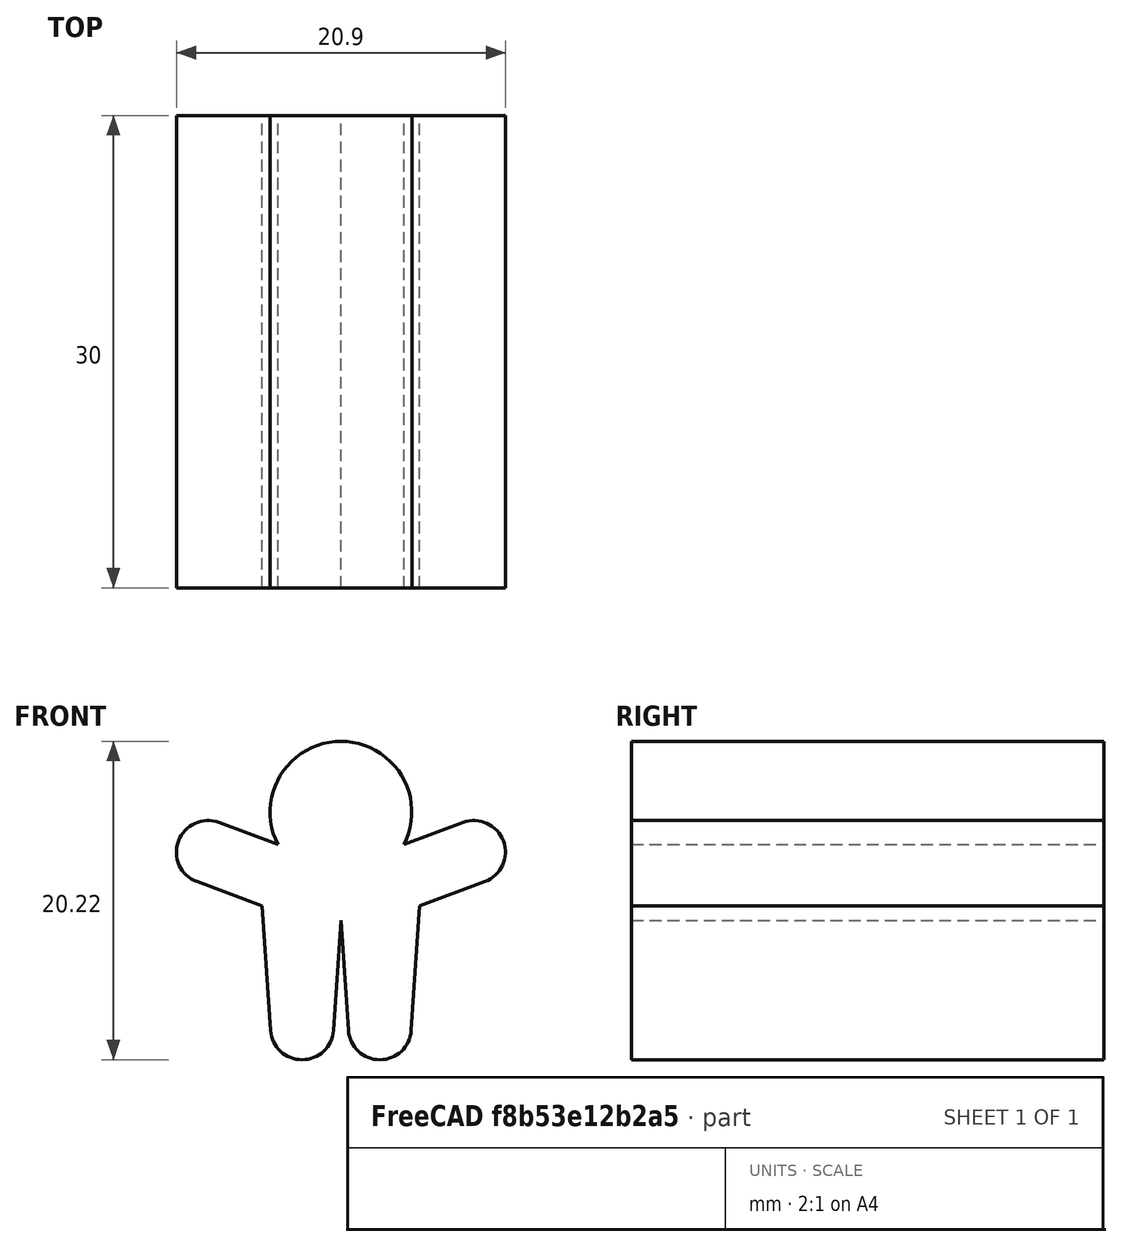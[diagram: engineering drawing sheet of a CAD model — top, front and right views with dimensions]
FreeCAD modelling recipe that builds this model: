
FCSTD DOCUMENT  (FreeCAD 0.17R13522 (Git))
Label: munieco
License: CreativeCommons Attribution-ShareAlike
LicenseURL: http://creativecommons.org/licenses/by-sa/4.0/
objects: Sketcher::SketchObject×1, Part::Extrusion×1, Part::Feature×1
note: 3 computed .brp shape members not serialized (recipe doc carries the construction recipe); baked Part::Feature solids carry a one-line shape summary decoded from their .brp

FEATURE [Sketcher::SketchObject] Sketch002
  MapMode = 5
  Placement = pos=(0,0,0) rot=(1,0,0;1.5708rad)
  Support = -> [XZ_Plane002]
  sketch-geometry (19):
    g0: LineSegment StartX=-5 StartY=10.9 StartZ=0 EndX=-4.46495 EndY=3 EndZ=0
    g1: LineSegment StartX=-0.474094 StartY=3 StartZ=0 EndX=0 EndY=10 EndZ=0
    g2: LineSegment StartX=0 StartY=10 StartZ=0 EndX=0.474094 EndY=3 EndZ=0
    g3: LineSegment StartX=5 StartY=10.9 StartZ=0 EndX=4.46495 EndY=3 EndZ=0
    g4: LineSegment [constr] StartX=-5 StartY=10.9 StartZ=0 EndX=5 EndY=10.9 EndZ=0
    g5: LineSegment [constr] StartX=-4.46495 StartY=3 StartZ=0 EndX=-0.474094 EndY=3 EndZ=0
    g6: LineSegment [constr] StartX=0.474094 StartY=3 StartZ=0 EndX=4.46495 EndY=3 EndZ=0
    g7: LineSegment StartX=-5 StartY=10.9 StartZ=0 EndX=-9.147 EndY=12.4495 EndZ=0
    g8: LineSegment StartX=-7.747 StartY=16.1965 StartZ=0 EndX=-4 EndY=14.7965 EndZ=0
    g9: LineSegment StartX=5 StartY=10.9 StartZ=0 EndX=9.147 EndY=12.4495 EndZ=0
    g10: LineSegment StartX=4 StartY=14.7965 StartZ=0 EndX=7.747 EndY=16.1965 EndZ=0
    g11: LineSegment [constr] StartX=-9.147 StartY=12.4495 StartZ=0 EndX=9.147 EndY=12.4495 EndZ=0
    g12: LineSegment [constr] StartX=-4 StartY=14.7965 StartZ=0 EndX=4 EndY=14.7965 EndZ=0
    g13: LineSegment [constr] StartX=-7.747 StartY=16.1965 StartZ=0 EndX=7.747 EndY=16.1965 EndZ=0
    g14: ArcOfCircle CenterX=0 CenterY=16.858 CenterZ=0 NormalX=0 NormalY=0 NormalZ=1 AngleXU=0 Radius=4.5 StartAngle=5.8073 EndAngle=9.90066
    g15: ArcOfCircle CenterX=8.447 CenterY=14.323 CenterZ=0 NormalX=0 NormalY=0 NormalZ=1 AngleXU=0 Radius=2 StartAngle=5.06996 EndAngle=8.21155
    g16: ArcOfCircle CenterX=-2.46952 CenterY=3.13515 CenterZ=0 NormalX=0 NormalY=0 NormalZ=1 AngleXU=0 Radius=2 StartAngle=3.20922 EndAngle=6.21556
    g17: ArcOfCircle CenterX=2.46952 CenterY=3.13515 CenterZ=0 NormalX=0 NormalY=0 NormalZ=1 AngleXU=0 Radius=2 StartAngle=3.20922 EndAngle=6.21556
    g18: ArcOfCircle CenterX=-8.447 CenterY=14.323 CenterZ=0 NormalX=0 NormalY=0 NormalZ=1 AngleXU=0 Radius=2 StartAngle=1.21323 EndAngle=4.35482
  constraints (50):
    c: Coincident(g4,g0)
    c: Coincident(g4,g3)
    c: Horizontal(g4)
    c: Coincident(g5,g0)
    c: Coincident(g5,g1)
    c: Coincident(g6,g2)
    c: Coincident(g6,g3)
    c: Horizontal(g6)
    c: Coincident(g7,g0)
    c: Coincident(g11,g7)
    c: Coincident(g11,g9)
    c: Horizontal(g11)
    c: Horizontal(g12)
    c: Coincident(g13,g8)
    c: Horizontal(g13)
    c: Coincident(g10,g13)
    c: Coincident(g12,g10)
    c: Coincident(g12,g8)
    c: Horizontal(g5)
    c: DistanceY(g2,g1) = 0
    c: DistanceY(g1,g2) = 0
    c: Coincident(g3,g9)
    c: Distance(g4) = 10
    c: Parallel(g7,g8)
    c: Parallel(g9,g10)
    c: DistanceX(g10,g3) = 1
    c: DistanceX(g0,g8) = 1
    c: Distance(g10) = 4
    c: Equal(g10,g8)
    c: Coincident(g14,g8)
    c: Coincident(g14,g10)
    c: Radius(g14) = 4.5
    c: Coincident(g15,g10)
    c: Tangent(g15,g9) = -1.5708
    c: Radius(g15) = 2
    c: Tangent(g16,g1) = -1.5708
    c: Tangent(g17,g2) = -1.5708
    c: Tangent(g0,g16) = -1.5708
    c: DistanceX(g0,g1) = 5
    c: DistanceX(g2,g3) = 5
    c: Tangent(g17,g3) = 1.5708
    c: Radius(g17) = 2
    c: Radius(g16) = 2
    c: DistanceY(g10,g10) = 1.4
    c: DistanceY(g3,g3) = 7.9
    c: DistanceX(g-1,g1) = 0
    c: DistanceY(g-1,g1) = 10
    c: DistanceY(g3,g1) = 7
    c: Tangent(g18,g7) = 1.5708
    c: Tangent(g18,g8) = 1.5708
FEATURE [Part::Extrusion] Extrude
  Base = -> Sketch002
  Dir = (0,-1,0)
  DirMode = 2
  FaceMakerClass = Part::FaceMakerBullseye
  LengthFwd = -30
  LengthRev = 0
  Solid = true
  Symmetric = false
FEATURE [Part::Feature] Extrude001
  shape: bbox 20.89 x 30 x 20.22 mm, 15 faces (baked)
